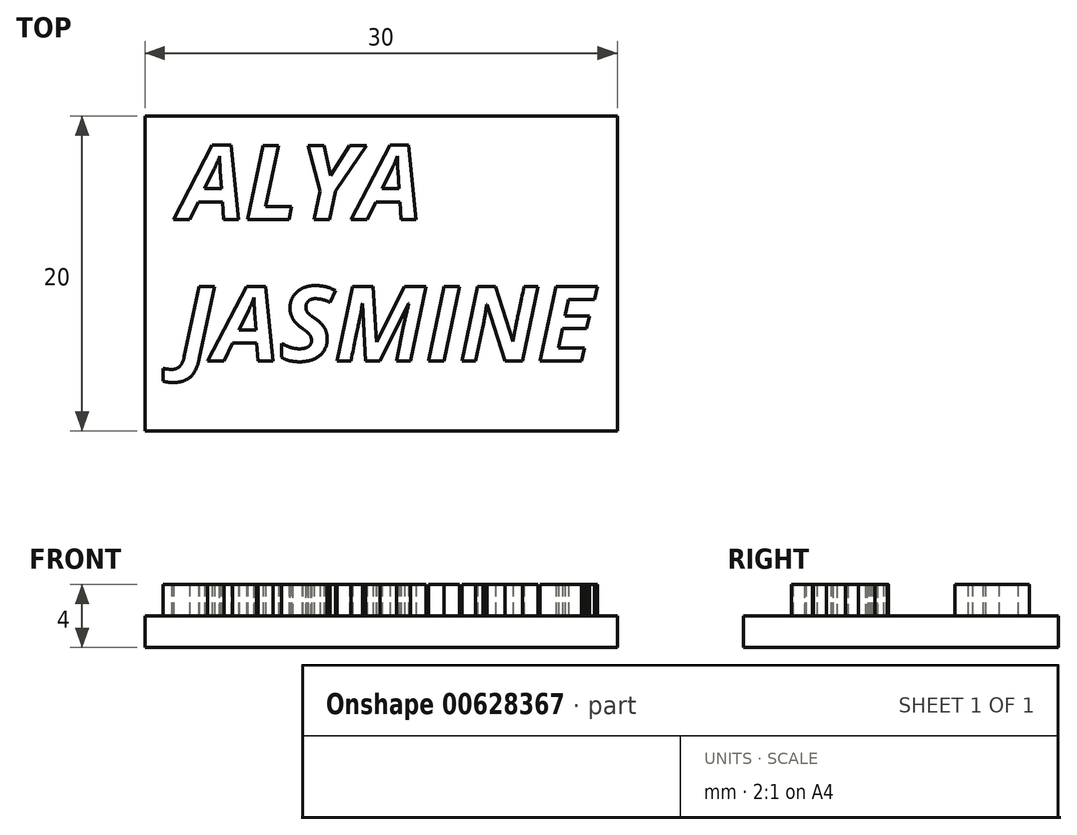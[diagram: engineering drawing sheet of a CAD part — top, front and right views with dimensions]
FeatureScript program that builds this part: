
annotation { "Feature Type Name" : "Feature", "Feature Type Description" : "" }
export const myFeature = defineFeature(function(context is Context, id is Id, definition is map)
    precondition{}
    {
        {
            var Q0;
            Q0=qCreatedBy(makeId("Top.planeOp"),FACE);
            var sketch = newSketch(context, id + "F0", { "sketchPlane" : qUnion([Q0])});
            skLineSegment(sketch, "E0.bottom", {"start": v(5.03, 0) * mm, "end": v(-24.97, 0) * mm});
            skLineSegment(sketch, "E0.top", {"start": v(5.03, 20) * mm, "end": v(-24.97, 20) * mm});
            skLineSegment(sketch, "E0.left", {"start": v(5.03, 0) * mm, "end": v(5.03, 20) * mm});
            skLineSegment(sketch, "E0.right", {"start": v(-24.97, 0) * mm, "end": v(-24.97, 20) * mm});
            skSolve(sketch);
        }
        {
            var Q0;
            Q0=makeQuery(id+"F0.imprint","IMPRINT",FACE,{"disambiguationData":[TD([[makeQuery(id+"F0.imprint","IMPRINT",EDGE,{"derivedFrom":sQuery(id+"F0.wireOp",EDGE,"E0.bottom")}),-1.0]])]});
            extrude(context, id + "F1", {"entities" : qUnion([Q0]), "depth" : 2 * mm, "offsetDistance" : 25.4 * mm});
        }
        {
            var Q0;
            Q0=makeQuery(id+"F1.opExtrude","CAP_FACE",FACE,{"disambiguationData":[OSD([sQuery(id+"F0.wireOp",EDGE,"E0.bottom"),sQuery(id+"F0.wireOp",EDGE,"E0.top"),sQuery(id+"F0.wireOp",EDGE,"E0.left"),sQuery(id+"F0.wireOp",EDGE,"E0.right")])],"isStart":false});
            var sketch = newSketch(context, id + "F2", { "sketchPlane" : qUnion([Q0])});
            skText(sketch, "E1", { "text": "ALYA \nJASMINE", "fontName": "OpenSans-BoldItalic.ttf"});
            const initialGuessF2  = {"E1": [-0.02277, 0.01343, 1, 0, 0.00475]};
            skSetInitialGuess(sketch, initialGuessF2);
            skSolve(sketch);
        }
        {
            var Q0;
            Q0 = qSketchRegion(id + "F2", true);
            extrude(context, id + "F3", {"entities" : qUnion([Q0]), "operationType" : NewBodyOperationType.ADD, "depth" : 2 * mm, "offsetDistance" : 25.4 * mm});
        }
    });
